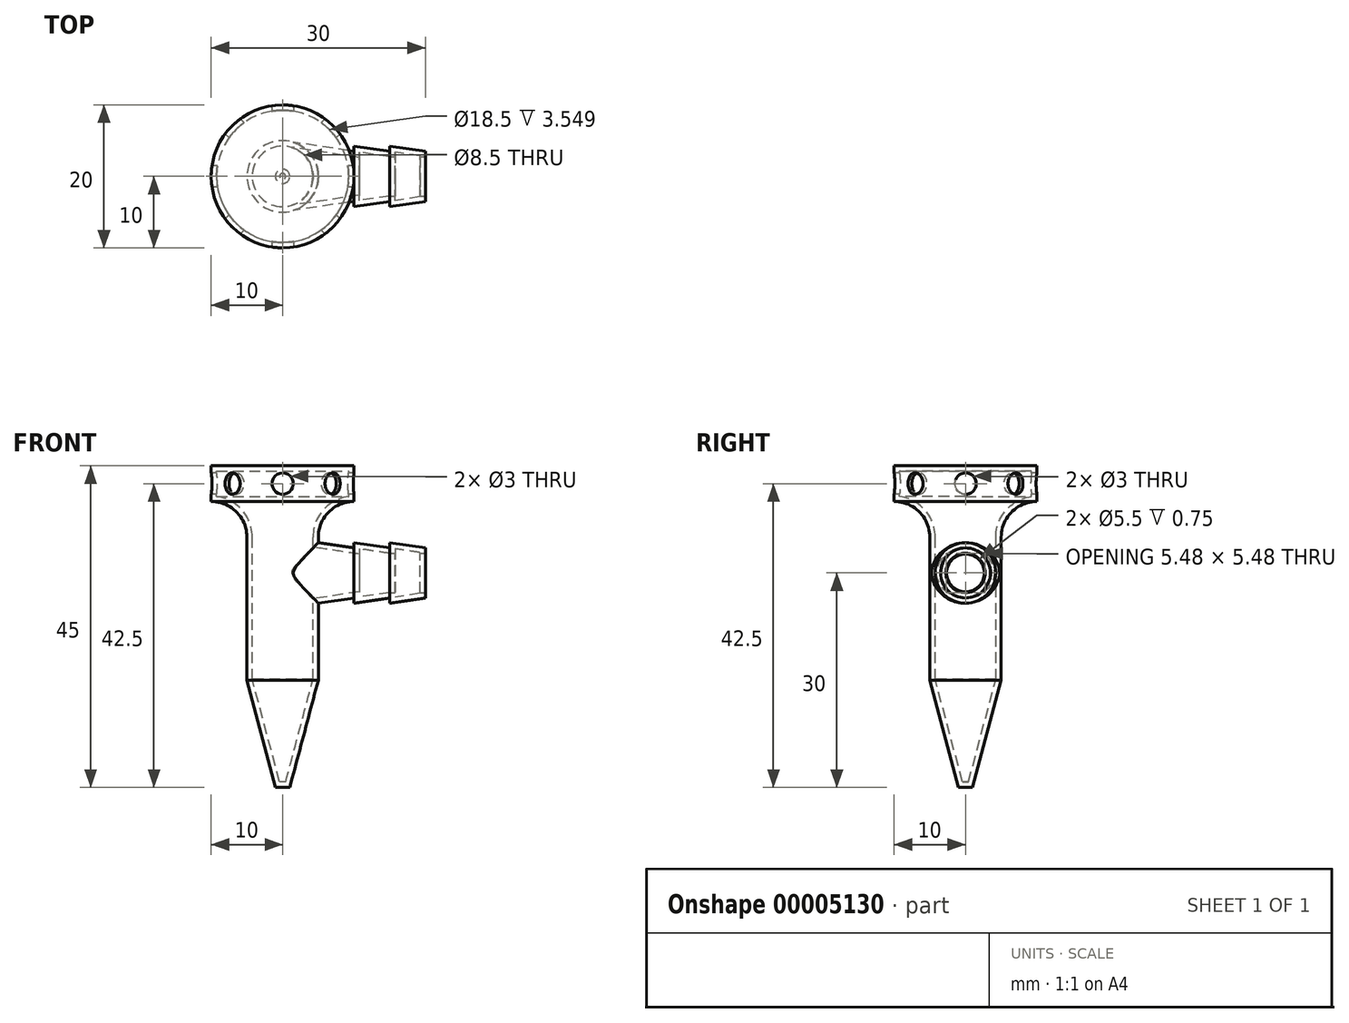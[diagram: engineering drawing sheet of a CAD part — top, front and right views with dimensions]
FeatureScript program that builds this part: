
annotation { "Feature Type Name" : "Feature", "Feature Type Description" : "" }
export const myFeature = defineFeature(function(context is Context, id is Id, definition is map)
    precondition{}
    {
        {
            var Q0;
            Q0=qCreatedBy(makeId("Front.planeOp"),FACE);
            var sketch = newSketch(context, id + "F0", { "sketchPlane" : qUnion([Q0])});
            skLineSegment(sketch, "E0", {"start": v(0, 0) * mm, "end": v(5, 0) * mm});
            skLineSegment(sketch, "E1", {"start": v(5, 0) * mm, "end": v(5, 35) * mm});
            skLineSegment(sketch, "E2", {"start": v(10, 40) * mm, "end": v(10, 45) * mm});
            skLineSegment(sketch, "E3", {"start": v(10, 45) * mm, "end": v(0, 45) * mm});
            skLineSegment(sketch, "E4", {"start": v(0, 45) * mm, "end": v(0, 0) * mm});
            skLineSegment(sketch, "E5", {"start": v(10, 40) * mm, "end": v(10, 40) * mm});
            skPoint(sketch, "E6.visualSharp", {"position": v(5, 40) * mm});
            skArc(sketch, "E6.filletArc", {"start": v(10, 40) * mm, "mid": v(6.46, 38.54) * mm, "end": v(5, 35) * mm});
            skSolve(sketch);
        }
        {
            var Q0;
            Q0=makeQuery(id+"F0.imprint","IMPRINT",FACE,{"disambiguationData":[TD([[makeQuery(id+"F0.imprint","IMPRINT",EDGE,{"derivedFrom":sQuery(id+"F0.wireOp",EDGE,"E0")}),1.0]])]});
            var Q1;
            Q1=sQuery(id+"F0.wireOp",EDGE,"E4");
            revolve(context, id + "F1", {"entities" : qUnion([Q0]), "axis" : qUnion([Q1]), "revolveType" : RevolveType.FULL});
        }
        {
            var Q0;
            Q0=makeQuery(id+"F1.opRevolve","SWEPT_EDGE",EDGE,{"disambiguationData":[OSD([sQuery(id+"F0.wireOp",EDGE,"E0"),sQuery(id+"F0.wireOp",EDGE,"E1")])]});
            chamfer(context, id + "F2", {"entities" : qUnion([Q0]), "chamferType" : ChamferType.TWO_OFFSETS, "width1" : 15 * mm, "oppositeDirection" : false, "width2" : 4 * mm, "tangentPropagation" : true});
        }
        {
            var Q0;
            Q0=qCreatedBy(makeId("Front.planeOp"),FACE);
            var sketch = newSketch(context, id + "F3", { "sketchPlane" : qUnion([Q0])});
            skCircle(sketch, "E7", {"center": v(0, 42.5) * mm, "radius": 1.5 * mm});
            skSolve(sketch);
        }
        {
            var Q0;
            Q0 = qSketchRegion(id + "F3", true);
            extrude(context, id + "F4", {"entities" : qUnion([Q0]), "depth" : 25 * mm});
        }
        {
            var Q0;
            Q0=qCreatedBy(makeId("Front.planeOp"),FACE);
            var sketch = newSketch(context, id + "F5", { "sketchPlane" : qUnion([Q0])});
            skLineSegment(sketch, "E8", {"start": v(20, 30) * mm, "end": v(20, 33.5) * mm});
            skLineSegment(sketch, "E9", {"start": v(20, 33.5) * mm, "end": v(15, 34.25) * mm});
            skLineSegment(sketch, "E10", {"start": v(15, 34.25) * mm, "end": v(15, 33.5) * mm});
            skLineSegment(sketch, "E11", {"start": v(15, 33.5) * mm, "end": v(10, 34.25) * mm});
            skLineSegment(sketch, "E12", {"start": v(10, 34.25) * mm, "end": v(10, 33.5) * mm});
            skLineSegment(sketch, "E13", {"start": v(10, 33.5) * mm, "end": v(0, 35) * mm});
            skLineSegment(sketch, "E14", {"start": v(10, 33.5) * mm, "end": v(15, 33.5) * mm, "construction": true});
            skLineSegment(sketch, "E15", {"start": v(20, 33.5) * mm, "end": v(15, 33.5) * mm, "construction": true});
            skLineSegment(sketch, "E16", {"start": v(20, 30) * mm, "end": v(0, 30) * mm});
            skLineSegment(sketch, "E17", {"start": v(0, 30) * mm, "end": v(0, 35) * mm});
            skSolve(sketch);
        }
        {
            var Q0;
            Q0=makeQuery(id+"F5.imprint","IMPRINT",FACE,{"disambiguationData":[TD([[makeQuery(id+"F5.imprint","IMPRINT",EDGE,{"derivedFrom":sQuery(id+"F5.wireOp",EDGE,"E8")}),1.0]])]});
            var Q1;
            Q1=sQuery(id+"F5.wireOp",EDGE,"E16");
            revolve(context, id + "F6", {"operationType" : NewBodyOperationType.ADD, "entities" : qUnion([Q0]), "axis" : qUnion([Q1]), "revolveType" : RevolveType.FULL});
        }
        {
            var Q0;
            Q0=makeQuery(id+"F1.opRevolve","SWEPT_FACE",FACE,{"disambiguationData":[OSD([sQuery(id+"F0.wireOp",EDGE,"E2")])]});
            var Q1;
            Q1=makeQuery(id+"F1.opRevolve","SWEPT_BODY",BODY,{"disambiguationData":[OSD([sQuery(id+"F0.wireOp",EDGE,"E0"),sQuery(id+"F0.wireOp",EDGE,"E1"),sQuery(id+"F0.wireOp",EDGE,"E2"),sQuery(id+"F0.wireOp",EDGE,"E3"),sQuery(id+"F0.wireOp",EDGE,"E4"),sQuery(id+"F0.wireOp",EDGE,"E6.filletArc")])]});
            shell(context, id + "F7", {"isHollow" : true, "entities" : qUnion([Q0]), "parts" : qUnion([Q1]), "thickness" : 0.75 * mm});
        }
        {
            var Q0;
            Q0=makeQuery(id+"F4.opExtrude","SWEPT_BODY",BODY,{"disambiguationData":[OSD([sQuery(id+"F3.wireOp",EDGE,"E7")])]});
            var Q1;
            Q1=sQuery(id+"F0.wireOp",EDGE,"E4");
            circularPattern(context, id + "F8", {"entities" : qUnion([Q0]), "axis" : qUnion([Q1]), "angle" : 45 * degree, "instanceCount" : 8});
        }
        {
            var Q0;
            Q0=makeQuery(id+"F8.opPattern","COPY",BODY,{"derivedFrom":makeQuery(id+"F4.opExtrude","SWEPT_BODY",BODY,{"disambiguationData":[OSD([sQuery(id+"F3.wireOp",EDGE,"E7")])]}),"instanceName":"5"});
            var Q1;
            Q1=makeQuery(id+"F8.opPattern","COPY",BODY,{"derivedFrom":makeQuery(id+"F4.opExtrude","SWEPT_BODY",BODY,{"disambiguationData":[OSD([sQuery(id+"F3.wireOp",EDGE,"E7")])]}),"instanceName":"6"});
            var Q2;
            Q2=makeQuery(id+"F8.opPattern","COPY",BODY,{"derivedFrom":makeQuery(id+"F4.opExtrude","SWEPT_BODY",BODY,{"disambiguationData":[OSD([sQuery(id+"F3.wireOp",EDGE,"E7")])]}),"instanceName":"7"});
            var Q3;
            Q3=makeQuery(id+"F8.opPattern","COPY",BODY,{"derivedFrom":makeQuery(id+"F4.opExtrude","SWEPT_BODY",BODY,{"disambiguationData":[OSD([sQuery(id+"F3.wireOp",EDGE,"E7")])]}),"instanceName":"1"});
            var Q4;
            Q4=makeQuery(id+"F8.opPattern","COPY",BODY,{"derivedFrom":makeQuery(id+"F4.opExtrude","SWEPT_BODY",BODY,{"disambiguationData":[OSD([sQuery(id+"F3.wireOp",EDGE,"E7")])]}),"instanceName":"2"});
            var Q5;
            Q5=makeQuery(id+"F8.opPattern","COPY",BODY,{"derivedFrom":makeQuery(id+"F4.opExtrude","SWEPT_BODY",BODY,{"disambiguationData":[OSD([sQuery(id+"F3.wireOp",EDGE,"E7")])]}),"instanceName":"3"});
            var Q6;
            Q6=makeQuery(id+"F8.opPattern","COPY",BODY,{"derivedFrom":makeQuery(id+"F4.opExtrude","SWEPT_BODY",BODY,{"disambiguationData":[OSD([sQuery(id+"F3.wireOp",EDGE,"E7")])]}),"instanceName":"4"});
            var Q7;
            Q7=makeQuery(id+"F4.opExtrude","SWEPT_BODY",BODY,{"disambiguationData":[OSD([sQuery(id+"F3.wireOp",EDGE,"E7")])]});
            var Q8;
            Q8=makeQuery(id+"F1.opRevolve","SWEPT_BODY",BODY,{"disambiguationData":[OSD([sQuery(id+"F0.wireOp",EDGE,"E0"),sQuery(id+"F0.wireOp",EDGE,"E1"),sQuery(id+"F0.wireOp",EDGE,"E2"),sQuery(id+"F0.wireOp",EDGE,"E3"),sQuery(id+"F0.wireOp",EDGE,"E4"),sQuery(id+"F0.wireOp",EDGE,"E6.filletArc")])]});
            booleanBodies(context, id + "F9", {"operationType" : BooleanOperationType.SUBTRACTION, "tools" : qUnion([Q0, Q1, Q2, Q3, Q4, Q5, Q6, Q7]), "targets" : qUnion([Q8])});
        }
        {
            var Q0;
            Q0=makeQuery(id+"F6.opRevolve","SWEPT_FACE",FACE,{"disambiguationData":[OSD([sQuery(id+"F5.wireOp",EDGE,"E8")])]});
            var sketch = newSketch(context, id + "F10", { "sketchPlane" : qUnion([Q0])});
            skCircle(sketch, "E18", {"center": v(0, 30) * mm, "radius": 2.75 * mm});
            skSolve(sketch);
        }
        {
            var Q0;
            Q0 = qSketchRegion(id + "F10", true);
            extrude(context, id + "F11", {"entities" : qUnion([Q0]), "operationType" : NewBodyOperationType.REMOVE, "oppositeDirection" : true, "depth" : 5 * mm});
        }
    });
